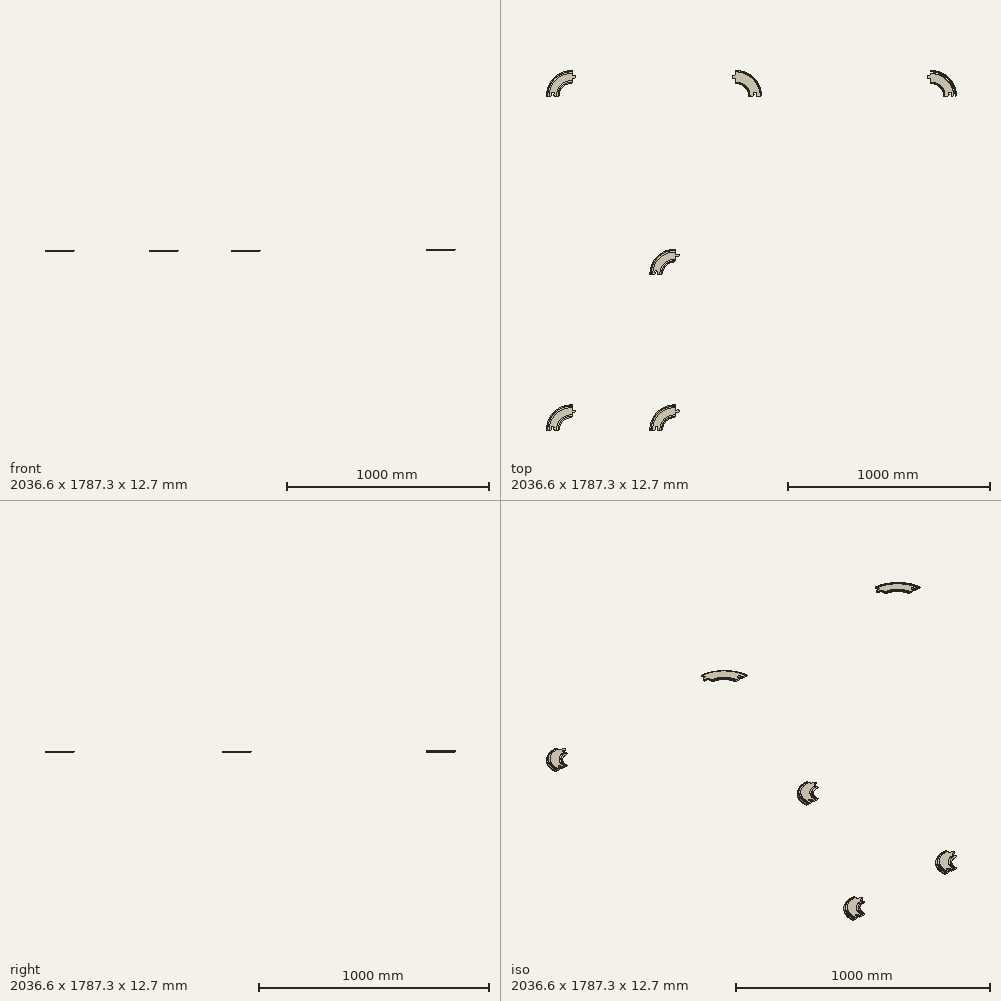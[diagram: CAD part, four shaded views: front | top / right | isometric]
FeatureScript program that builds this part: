
annotation { "Feature Type Name" : "Feature", "Feature Type Description" : "" }
export const myFeature = defineFeature(function(context is Context, id is Id, definition is map)
    precondition{}
    {
        {
            var Q0;
            Q0=qCreatedBy(makeId("Top.planeOp"),FACE);
            var sketch = newSketch(context, id + "F0", { "sketchPlane" : qUnion([Q0])});
            skArc(sketch, "E0", {"start": v(0, 127) * mm, "mid": v(-89.8, 89.8) * mm, "end": v(-127, 0) * mm});
            skArc(sketch, "E1.0", {"start": v(0, 63.5) * mm, "mid": v(-44.9, 44.9) * mm, "end": v(-63.5, 0) * mm});
            skLineSegment(sketch, "E2", {"start": v(-127, 0) * mm, "end": v(-101.6, 0) * mm});
            skLineSegment(sketch, "E3", {"start": v(0, 63.5) * mm, "end": v(0, 88.9) * mm});
            skArc(sketch, "E4", {"start": v(12.7, 88.9) * mm, "mid": v(19.05, 95.25) * mm, "end": v(12.7, 101.6) * mm});
            skPoint(sketch, "E5.start.orphan", {"position": v(12.7, 62.67) * mm});
            skArc(sketch, "E6", {"start": v(12.7, 88.9) * mm, "mid": v(6.35, 90.29) * mm, "end": v(0, 88.9) * mm});
            skArc(sketch, "E7.MirrorCS", {"start": v(12.7, 101.6) * mm, "mid": v(6.35, 100.21) * mm, "end": v(0, 101.6) * mm});
            skArc(sketch, "E8", {"start": v(-88.9, 12.7) * mm, "mid": v(-95.25, 19.05) * mm, "end": v(-101.6, 12.7) * mm});
            skLineSegment(sketch, "E9", {"start": v(-101.6, 12.7) * mm, "end": v(-102.39, 12.7) * mm});
            skPoint(sketch, "E10.startSnap0", {"position": v(-102.39, 12.7) * mm});
            skPoint(sketch, "E11.orphan", {"position": v(-71.93, 12.7) * mm});
            skLineSegment(sketch, "E12.trimOffspring", {"start": v(-126.36, 12.7) * mm, "end": v(-132.85, 12.7) * mm});
            skArc(sketch, "E13", {"start": v(-88.9, 12.7) * mm, "mid": v(-90.29, 6.35) * mm, "end": v(-88.9, 0) * mm});
            skArc(sketch, "E14.MirrorCS", {"start": v(-101.6, 12.7) * mm, "mid": v(-100.21, 6.35) * mm, "end": v(-101.6, 0) * mm});
            skPoint(sketch, "E10.end.orphan", {"position": v(-101.6, 0) * mm});
            skLineSegment(sketch, "E15.trimOffspring", {"start": v(0, 101.6) * mm, "end": v(0, 127) * mm});
            skLineSegment(sketch, "E16.trimOffspring", {"start": v(-88.9, 0) * mm, "end": v(-63.5, 0) * mm});
            skLineSegment(sketch, "E17", {"start": v(76.77, 161.45) * mm, "end": v(76.77, -32.66) * mm});
            skLineSegment(sketch, "E18", {"start": v(333.5, 184.4) * mm, "end": v(333.5, -54.92) * mm});
            skLineSegment(sketch, "E19.MirrorCS", {"start": v(411.86, 12.7) * mm, "end": v(411.07, 12.7) * mm});
            skArc(sketch, "E20.MirrorCS", {"start": v(526.16, 88.9) * mm, "mid": v(519.8, 90.29) * mm, "end": v(513.46, 88.9) * mm});
            skArc(sketch, "E21.MirrorCS", {"start": v(526.16, 101.6) * mm, "mid": v(519.8, 100.21) * mm, "end": v(513.46, 101.6) * mm});
            skArc(sketch, "E22.MirrorCS", {"start": v(411.86, 12.7) * mm, "mid": v(413.24, 6.35) * mm, "end": v(411.86, 0) * mm});
            skArc(sketch, "E23.MirrorCS", {"start": v(424.56, 12.7) * mm, "mid": v(418.2, 19.05) * mm, "end": v(411.86, 12.7) * mm});
            skArc(sketch, "E24.MirrorCS", {"start": v(526.16, 88.9) * mm, "mid": v(532.5, 95.25) * mm, "end": v(526.16, 101.6) * mm});
            skLineSegment(sketch, "E25.MirrorCS", {"start": v(513.46, 63.5) * mm, "end": v(513.46, 88.9) * mm});
            skArc(sketch, "E26.MirrorCS", {"start": v(424.56, 12.7) * mm, "mid": v(423.17, 6.35) * mm, "end": v(424.56, 0) * mm});
            skLineSegment(sketch, "E27.MirrorCS", {"start": v(513.46, 101.6) * mm, "end": v(513.46, 127) * mm});
            skLineSegment(sketch, "E28.MirrorCS", {"start": v(424.56, 0) * mm, "end": v(449.96, 0) * mm});
            skPoint(sketch, "E29.MirrorP", {"position": v(526.16, 62.67) * mm});
            skLineSegment(sketch, "E30.MirrorCS", {"start": v(387.1, 12.7) * mm, "end": v(380.6, 12.7) * mm});
            skLineSegment(sketch, "E31.MirrorCS", {"start": v(386.46, 0) * mm, "end": v(411.86, 0) * mm});
            skPoint(sketch, "E32.MirrorP", {"position": v(411.07, 12.7) * mm});
            skArc(sketch, "E33.MirrorCS", {"start": v(513.46, 127) * mm, "mid": v(423.65, 89.8) * mm, "end": v(386.46, 0) * mm});
            skPoint(sketch, "E34.MirrorP", {"position": v(411.86, 0) * mm});
            skArc(sketch, "E35.MirrorCS", {"start": v(513.46, 63.5) * mm, "mid": v(468.55, 44.9) * mm, "end": v(449.96, 0) * mm});
            skPoint(sketch, "E36.MirrorP", {"position": v(441.53, 12.7) * mm});
            skLineSegment(sketch, "E37.MirrorCS", {"start": v(-101.6, -874.4) * mm, "end": v(-102.39, -874.4) * mm});
            skLineSegment(sketch, "E38.MirrorCS", {"start": v(411.86, -874.4) * mm, "end": v(411.07, -874.4) * mm});
            skArc(sketch, "E39.MirrorCS", {"start": v(424.56, -874.4) * mm, "mid": v(423.17, -880.75) * mm, "end": v(424.56, -887.1) * mm});
            skArc(sketch, "E40.MirrorCS", {"start": v(526.16, -785.5) * mm, "mid": v(519.8, -786.88) * mm, "end": v(513.46, -785.5) * mm});
            skArc(sketch, "E41.MirrorCS", {"start": v(-101.6, -874.4) * mm, "mid": v(-100.21, -880.75) * mm, "end": v(-101.6, -887.1) * mm});
            skArc(sketch, "E42.MirrorCS", {"start": v(424.56, -874.4) * mm, "mid": v(418.2, -868.05) * mm, "end": v(411.86, -874.4) * mm});
            skArc(sketch, "E43.MirrorCS", {"start": v(526.16, -798.2) * mm, "mid": v(519.8, -796.81) * mm, "end": v(513.46, -798.2) * mm});
            skArc(sketch, "E44.MirrorCS", {"start": v(411.86, -874.4) * mm, "mid": v(413.24, -880.75) * mm, "end": v(411.86, -887.1) * mm});
            skArc(sketch, "E45.MirrorCS", {"start": v(-88.9, -874.4) * mm, "mid": v(-90.29, -880.75) * mm, "end": v(-88.9, -887.1) * mm});
            skArc(sketch, "E46.MirrorCS", {"start": v(-88.9, -874.4) * mm, "mid": v(-95.25, -868.05) * mm, "end": v(-101.6, -874.4) * mm});
            skLineSegment(sketch, "E47.MirrorCS", {"start": v(424.56, -887.1) * mm, "end": v(449.96, -887.1) * mm});
            skArc(sketch, "E48.MirrorCS", {"start": v(526.16, -798.2) * mm, "mid": v(532.5, -791.85) * mm, "end": v(526.16, -785.5) * mm});
            skArc(sketch, "E49.MirrorCS", {"start": v(12.7, -798.2) * mm, "mid": v(19.05, -791.85) * mm, "end": v(12.7, -785.5) * mm});
            skArc(sketch, "E50.MirrorCS", {"start": v(12.7, -785.5) * mm, "mid": v(6.35, -786.88) * mm, "end": v(0, -785.5) * mm});
            skArc(sketch, "E51.MirrorCS", {"start": v(12.7, -798.2) * mm, "mid": v(6.35, -796.81) * mm, "end": v(0, -798.2) * mm});
            skLineSegment(sketch, "E52.MirrorCS", {"start": v(-127, -887.1) * mm, "end": v(-101.6, -887.1) * mm});
            skLineSegment(sketch, "E53.MirrorCS", {"start": v(-88.9, -887.1) * mm, "end": v(-63.5, -887.1) * mm});
            skLineSegment(sketch, "E54.MirrorCS", {"start": v(-126.36, -874.4) * mm, "end": v(-132.85, -874.4) * mm});
            skLineSegment(sketch, "E55.MirrorCS", {"start": v(513.46, -823.6) * mm, "end": v(513.46, -798.2) * mm});
            skLineSegment(sketch, "E56.MirrorCS", {"start": v(387.1, -874.4) * mm, "end": v(380.6, -874.4) * mm});
            skLineSegment(sketch, "E57.MirrorCS", {"start": v(513.46, -785.5) * mm, "end": v(513.46, -760.1) * mm});
            skLineSegment(sketch, "E58.MirrorCS", {"start": v(0, -785.5) * mm, "end": v(0, -760.1) * mm});
            skLineSegment(sketch, "E59.MirrorCS", {"start": v(0, -823.6) * mm, "end": v(0, -798.2) * mm});
            skLineSegment(sketch, "E60.MirrorCS", {"start": v(386.46, -887.1) * mm, "end": v(411.86, -887.1) * mm});
            skPoint(sketch, "E61.MirrorP", {"position": v(526.16, -824.42) * mm});
            skPoint(sketch, "E62.MirrorP", {"position": v(-71.93, -874.4) * mm});
            skPoint(sketch, "E63.MirrorP", {"position": v(-101.6, -887.1) * mm});
            skArc(sketch, "E64.MirrorCS", {"start": v(0, -823.6) * mm, "mid": v(-44.9, -842.2) * mm, "end": v(-63.5, -887.1) * mm});
            skLineSegment(sketch, "E65.MirrorCS", {"start": v(333.5, -702.69) * mm, "end": v(333.5, -942.02) * mm});
            skArc(sketch, "E66.MirrorCS", {"start": v(513.46, -823.6) * mm, "mid": v(468.55, -842.2) * mm, "end": v(449.96, -887.1) * mm});
            skArc(sketch, "E67.MirrorCS", {"start": v(513.46, -760.1) * mm, "mid": v(423.65, -797.3) * mm, "end": v(386.46, -887.1) * mm});
            skPoint(sketch, "E68.MirrorP", {"position": v(411.86, -887.1) * mm});
            skPoint(sketch, "E69.MirrorP", {"position": v(441.53, -874.4) * mm});
            skArc(sketch, "E70.MirrorCS", {"start": v(0, -760.1) * mm, "mid": v(-89.8, -797.3) * mm, "end": v(-127, -887.1) * mm});
            skPoint(sketch, "E71.MirrorP", {"position": v(12.7, -824.42) * mm});
            skPoint(sketch, "E72.MirrorP", {"position": v(-102.39, -874.4) * mm});
            skLineSegment(sketch, "E73.MirrorCS", {"start": v(76.77, -725.65) * mm, "end": v(76.77, -919.76) * mm});
            skPoint(sketch, "E74.MirrorP", {"position": v(411.07, -874.4) * mm});
            skLineSegment(sketch, "E75.MirrorCS", {"start": v(411.86, -1647.6) * mm, "end": v(411.07, -1647.6) * mm});
            skArc(sketch, "E76.MirrorCS", {"start": v(424.56, -1647.6) * mm, "mid": v(418.2, -1641.26) * mm, "end": v(411.86, -1647.6) * mm});
            skArc(sketch, "E77.MirrorCS", {"start": v(424.56, -1647.6) * mm, "mid": v(423.17, -1653.96) * mm, "end": v(424.56, -1660.3) * mm});
            skArc(sketch, "E78.MirrorCS", {"start": v(411.86, -1647.6) * mm, "mid": v(413.24, -1653.96) * mm, "end": v(411.86, -1660.3) * mm});
            skLineSegment(sketch, "E79.MirrorCS", {"start": v(386.46, -1660.3) * mm, "end": v(411.86, -1660.3) * mm});
            skArc(sketch, "E80.MirrorCS", {"start": v(-88.9, -1647.6) * mm, "mid": v(-90.29, -1653.96) * mm, "end": v(-88.9, -1660.3) * mm});
            skLineSegment(sketch, "E81.MirrorCS", {"start": v(-127, -1660.3) * mm, "end": v(-101.6, -1660.3) * mm});
            skLineSegment(sketch, "E82.MirrorCS", {"start": v(-101.6, -1647.6) * mm, "end": v(-102.39, -1647.6) * mm});
            skArc(sketch, "E83.MirrorCS", {"start": v(-101.6, -1647.6) * mm, "mid": v(-100.21, -1653.96) * mm, "end": v(-101.6, -1660.3) * mm});
            skArc(sketch, "E84.MirrorCS", {"start": v(-88.9, -1647.6) * mm, "mid": v(-95.25, -1641.26) * mm, "end": v(-101.6, -1647.6) * mm});
            skArc(sketch, "E85.MirrorCS", {"start": v(526.16, -1571.4) * mm, "mid": v(519.8, -1570.02) * mm, "end": v(513.46, -1571.4) * mm});
            skArc(sketch, "E86.MirrorCS", {"start": v(526.16, -1558.7) * mm, "mid": v(519.8, -1560.1) * mm, "end": v(513.46, -1558.7) * mm});
            skLineSegment(sketch, "E87.MirrorCS", {"start": v(513.46, -1596.8) * mm, "end": v(513.46, -1571.4) * mm});
            skArc(sketch, "E88.MirrorCS", {"start": v(526.16, -1571.4) * mm, "mid": v(532.5, -1565.06) * mm, "end": v(526.16, -1558.7) * mm});
            skArc(sketch, "E89.MirrorCS", {"start": v(12.7, -1571.4) * mm, "mid": v(19.05, -1565.06) * mm, "end": v(12.7, -1558.7) * mm});
            skArc(sketch, "E90.MirrorCS", {"start": v(12.7, -1571.4) * mm, "mid": v(6.35, -1570.02) * mm, "end": v(0, -1571.4) * mm});
            skArc(sketch, "E91.MirrorCS", {"start": v(12.7, -1558.7) * mm, "mid": v(6.35, -1560.1) * mm, "end": v(0, -1558.7) * mm});
            skLineSegment(sketch, "E92.MirrorCS", {"start": v(-88.9, -1660.3) * mm, "end": v(-63.5, -1660.3) * mm});
            skLineSegment(sketch, "E93.MirrorCS", {"start": v(424.56, -1660.3) * mm, "end": v(449.96, -1660.3) * mm});
            skLineSegment(sketch, "E94.MirrorCS", {"start": v(513.46, -1558.7) * mm, "end": v(513.46, -1533.3) * mm});
            skLineSegment(sketch, "E95.MirrorCS", {"start": v(0, -1596.8) * mm, "end": v(0, -1571.4) * mm});
            skLineSegment(sketch, "E96.MirrorCS", {"start": v(-126.36, -1647.6) * mm, "end": v(-132.85, -1647.6) * mm});
            skLineSegment(sketch, "E97.MirrorCS", {"start": v(387.1, -1647.6) * mm, "end": v(380.6, -1647.6) * mm});
            skLineSegment(sketch, "E98.MirrorCS", {"start": v(0, -1558.7) * mm, "end": v(0, -1533.3) * mm});
            skPoint(sketch, "E99.MirrorP", {"position": v(526.16, -1597.64) * mm});
            skArc(sketch, "E100.MirrorCS", {"start": v(0, -1533.3) * mm, "mid": v(-89.8, -1570.5) * mm, "end": v(-127, -1660.3) * mm});
            skPoint(sketch, "E101.MirrorP", {"position": v(441.53, -1647.6) * mm});
            skArc(sketch, "E102.MirrorCS", {"start": v(513.46, -1596.8) * mm, "mid": v(468.55, -1615.4) * mm, "end": v(449.96, -1660.3) * mm});
            skPoint(sketch, "E103.MirrorP", {"position": v(411.07, -1647.6) * mm});
            skPoint(sketch, "E104.MirrorP", {"position": v(411.86, -1660.3) * mm});
            skPoint(sketch, "E105.MirrorP", {"position": v(-71.93, -1647.6) * mm});
            skPoint(sketch, "E106.MirrorP", {"position": v(-102.39, -1647.6) * mm});
            skLineSegment(sketch, "E107.MirrorCS", {"start": v(333.5, -1475.9) * mm, "end": v(333.5, -1715.23) * mm});
            skPoint(sketch, "E108.MirrorP", {"position": v(-101.6, -1660.3) * mm});
            skArc(sketch, "E109.MirrorCS", {"start": v(513.46, -1533.3) * mm, "mid": v(423.65, -1570.5) * mm, "end": v(386.46, -1660.3) * mm});
            skLineSegment(sketch, "E110.MirrorCS", {"start": v(76.77, -1498.86) * mm, "end": v(76.77, -1692.97) * mm});
            skPoint(sketch, "E111.MirrorP", {"position": v(12.7, -1597.64) * mm});
            skArc(sketch, "E112.MirrorCS", {"start": v(0, -1596.8) * mm, "mid": v(-44.9, -1615.4) * mm, "end": v(-63.5, -1660.3) * mm});
            skLineSegment(sketch, "E113", {"start": v(663.76, 185.94) * mm, "end": v(663.76, -109.84) * mm});
            skLineSegment(sketch, "E114", {"start": v(308.83, -128.2) * mm, "end": v(873.87, -128.2) * mm});
            skArc(sketch, "E115.MirrorCS", {"start": v(915.67, 12.7) * mm, "mid": v(914.28, 6.35) * mm, "end": v(915.67, 0) * mm});
            skArc(sketch, "E116.MirrorCS", {"start": v(902.97, 12.7) * mm, "mid": v(909.32, 19.05) * mm, "end": v(915.67, 12.7) * mm});
            skArc(sketch, "E117.MirrorCS", {"start": v(902.97, 12.7) * mm, "mid": v(904.35, 6.35) * mm, "end": v(902.97, 0) * mm});
            skLineSegment(sketch, "E118.MirrorCS", {"start": v(915.67, 12.7) * mm, "end": v(916.46, 12.7) * mm});
            skArc(sketch, "E119.MirrorCS", {"start": v(801.37, 88.9) * mm, "mid": v(807.72, 90.29) * mm, "end": v(814.07, 88.9) * mm});
            skArc(sketch, "E120.MirrorCS", {"start": v(801.37, 101.6) * mm, "mid": v(807.72, 100.21) * mm, "end": v(814.07, 101.6) * mm});
            skLineSegment(sketch, "E121.MirrorCS", {"start": v(814.07, 63.5) * mm, "end": v(814.07, 88.9) * mm});
            skArc(sketch, "E122.MirrorCS", {"start": v(801.37, 88.9) * mm, "mid": v(795.02, 95.25) * mm, "end": v(801.37, 101.6) * mm});
            skLineSegment(sketch, "E123.MirrorCS", {"start": v(814.07, 101.6) * mm, "end": v(814.07, 127) * mm});
            skLineSegment(sketch, "E124.MirrorCS", {"start": v(941.07, 0) * mm, "end": v(915.67, 0) * mm});
            skLineSegment(sketch, "E125.MirrorCS", {"start": v(902.97, 0) * mm, "end": v(877.57, 0) * mm});
            skLineSegment(sketch, "E126.MirrorCS", {"start": v(940.43, 12.7) * mm, "end": v(946.92, 12.7) * mm});
            skPoint(sketch, "E127.MirrorP", {"position": v(801.37, 62.67) * mm});
            skPoint(sketch, "E128.MirrorP", {"position": v(916.46, 12.7) * mm});
            skArc(sketch, "E129.MirrorCS", {"start": v(814.07, 63.5) * mm, "mid": v(858.97, 44.9) * mm, "end": v(877.57, 0) * mm});
            skArc(sketch, "E130.MirrorCS", {"start": v(814.07, 127) * mm, "mid": v(903.87, 89.8) * mm, "end": v(941.07, 0) * mm});
            skPoint(sketch, "E131.MirrorP", {"position": v(915.67, 0) * mm});
            skPoint(sketch, "E132.MirrorP", {"position": v(886, 12.7) * mm});
            skArc(sketch, "E133.MirrorCS", {"start": v(424.56, -269.1) * mm, "mid": v(423.17, -262.75) * mm, "end": v(424.56, -256.4) * mm});
            skArc(sketch, "E134.MirrorCS", {"start": v(526.16, -345.3) * mm, "mid": v(519.8, -346.68) * mm, "end": v(513.46, -345.3) * mm});
            skArc(sketch, "E135.MirrorCS", {"start": v(411.86, -269.1) * mm, "mid": v(413.24, -262.75) * mm, "end": v(411.86, -256.4) * mm});
            skLineSegment(sketch, "E136.MirrorCS", {"start": v(411.86, -269.1) * mm, "end": v(411.07, -269.1) * mm});
            skArc(sketch, "E137.MirrorCS", {"start": v(526.16, -358) * mm, "mid": v(519.8, -356.61) * mm, "end": v(513.46, -358) * mm});
            skArc(sketch, "E138.MirrorCS", {"start": v(424.56, -269.1) * mm, "mid": v(418.2, -275.45) * mm, "end": v(411.86, -269.1) * mm});
            skArc(sketch, "E139.MirrorCS", {"start": v(526.16, -345.3) * mm, "mid": v(532.5, -351.65) * mm, "end": v(526.16, -358) * mm});
            skLineSegment(sketch, "E140.MirrorCS", {"start": v(424.56, -256.4) * mm, "end": v(449.96, -256.4) * mm});
            skLineSegment(sketch, "E141.MirrorCS", {"start": v(513.46, -319.9) * mm, "end": v(513.46, -345.3) * mm});
            skLineSegment(sketch, "E142.MirrorCS", {"start": v(387.1, -269.1) * mm, "end": v(380.6, -269.1) * mm});
            skLineSegment(sketch, "E143.MirrorCS", {"start": v(386.46, -256.4) * mm, "end": v(411.86, -256.4) * mm});
            skLineSegment(sketch, "E144.MirrorCS", {"start": v(513.46, -358) * mm, "end": v(513.46, -383.4) * mm});
            skPoint(sketch, "E145.MirrorP", {"position": v(526.16, -319.07) * mm});
            skArc(sketch, "E146.MirrorCS", {"start": v(513.46, -383.4) * mm, "mid": v(423.65, -346.2) * mm, "end": v(386.46, -256.4) * mm});
            skArc(sketch, "E147.MirrorCS", {"start": v(513.46, -319.9) * mm, "mid": v(468.55, -301.3) * mm, "end": v(449.96, -256.4) * mm});
            skPoint(sketch, "E148.MirrorP", {"position": v(411.86, -256.4) * mm});
            skPoint(sketch, "E149.MirrorP", {"position": v(441.53, -269.1) * mm});
            skPoint(sketch, "E150.MirrorP", {"position": v(411.07, -269.1) * mm});
            skSolve(sketch);
        }
        {
            var Q0;
            Q0=makeQuery(id+"F0.imprint","IMPRINT",FACE,{"disambiguationData":[TD([[makeQuery(id+"F0.imprint","IMPRINT",EDGE,{"derivedFrom":sQuery(id+"F0.wireOp",EDGE,"E1.0")}),-1.0]])]});
            var Q1;
            Q1=makeQuery(id+"F0.imprint","IMPRINT",FACE,{"disambiguationData":[TD([[makeQuery(id+"F0.imprint","IMPRINT",EDGE,{"derivedFrom":sQuery(id+"F0.wireOp",EDGE,"E22.MirrorCS")}),-1.0]])]});
            var Q2;
            Q2=makeQuery(id+"F0.imprint","IMPRINT",FACE,{"disambiguationData":[TD([[makeQuery(id+"F0.imprint","IMPRINT",EDGE,{"derivedFrom":sQuery(id+"F0.wireOp",EDGE,"E39.MirrorCS")}),1.0]])]});
            var Q3;
            Q3=makeQuery(id+"F0.imprint","IMPRINT",FACE,{"disambiguationData":[TD([[makeQuery(id+"F0.imprint","IMPRINT",EDGE,{"derivedFrom":sQuery(id+"F0.wireOp",EDGE,"E41.MirrorCS")}),-1.0]])]});
            var Q4;
            Q4=makeQuery(id+"F0.imprint","IMPRINT",FACE,{"disambiguationData":[TD([[makeQuery(id+"F0.imprint","IMPRINT",EDGE,{"derivedFrom":sQuery(id+"F0.wireOp",EDGE,"E80.MirrorCS")}),1.0]])]});
            var Q5;
            Q5=makeQuery(id+"F0.imprint","IMPRINT",FACE,{"disambiguationData":[TD([[makeQuery(id+"F0.imprint","IMPRINT",EDGE,{"derivedFrom":sQuery(id+"F0.wireOp",EDGE,"E115.MirrorCS")}),1.0]])]});
            var Q6;
            Q6=makeQuery(id+"F0.imprint","IMPRINT",FACE,{"disambiguationData":[TD([[makeQuery(id+"F0.imprint","IMPRINT",EDGE,{"derivedFrom":sQuery(id+"F0.wireOp",EDGE,"E133.MirrorCS")}),-1.0]])]});
            var Q7;
            Q7=makeQuery(id+"F0.imprint","IMPRINT",FACE,{"disambiguationData":[TD([[makeQuery(id+"F0.imprint","IMPRINT",EDGE,{"derivedFrom":sQuery(id+"F0.wireOp",EDGE,"E76.MirrorCS")}),-1.0]])]});
            extrude(context, id + "F1", {"entities" : qUnion([Q0, Q1, Q2, Q3, Q4, Q5, Q6, Q7]), "depth" : 6.35 * mm});
        }
        {
            var Q0;
            Q0=makeQuery(id+"F1.opExtrude","CAP_FACE",FACE,{"disambiguationData":[OSD([sQuery(id+"F0.wireOp",EDGE,"E0"),sQuery(id+"F0.wireOp",EDGE,"E1.0"),sQuery(id+"F0.wireOp",EDGE,"E2"),sQuery(id+"F0.wireOp",EDGE,"E3"),sQuery(id+"F0.wireOp",EDGE,"E4"),sQuery(id+"F0.wireOp",EDGE,"E6"),sQuery(id+"F0.wireOp",EDGE,"E7.MirrorCS"),sQuery(id+"F0.wireOp",EDGE,"E8"),sQuery(id+"F0.wireOp",EDGE,"E13"),sQuery(id+"F0.wireOp",EDGE,"E14.MirrorCS"),sQuery(id+"F0.wireOp",EDGE,"E15.trimOffspring"),sQuery(id+"F0.wireOp",EDGE,"E16.trimOffspring")])],"isStart":false});
            var sketch = newSketch(context, id + "F2", { "sketchPlane" : qUnion([Q0])});
            skArc(sketch, "E151.0", {"start": v(0, 63.5) * mm, "mid": v(-44.9, 44.9) * mm, "end": v(-63.5, 0) * mm});
            skArc(sketch, "E151.1", {"start": v(0, 127) * mm, "mid": v(-89.8, 89.8) * mm, "end": v(-127, 0) * mm});
            skLineSegment(sketch, "E152.0", {"start": v(76.77, 161.45) * mm, "end": v(76.77, -32.66) * mm});
            skLineSegment(sketch, "E152.1", {"start": v(333.5, 184.4) * mm, "end": v(333.5, -54.92) * mm});
            skArc(sketch, "E153.0", {"start": v(0, 69.85) * mm, "mid": v(-49.4, 49.4) * mm, "end": v(-69.85, 0) * mm});
            skArc(sketch, "E154.0", {"start": v(0, 77.47) * mm, "mid": v(-54.78, 54.78) * mm, "end": v(-77.47, 0) * mm});
            skArc(sketch, "E155.0", {"start": v(0, 120.65) * mm, "mid": v(-85.31, 85.31) * mm, "end": v(-120.65, 0) * mm});
            skArc(sketch, "E156.0", {"start": v(0, 113.03) * mm, "mid": v(-79.92, 79.92) * mm, "end": v(-113.03, 0) * mm});
            skArc(sketch, "E157.MirrorCS", {"start": v(153.53, 113.03) * mm, "mid": v(233.46, 79.92) * mm, "end": v(266.56, 0) * mm});
            skArc(sketch, "E158.MirrorCS", {"start": v(153.53, 120.65) * mm, "mid": v(238.85, 85.31) * mm, "end": v(274.18, 0) * mm});
            skArc(sketch, "E159.MirrorCS", {"start": v(153.53, 69.85) * mm, "mid": v(202.93, 49.4) * mm, "end": v(223.38, 0) * mm});
            skArc(sketch, "E160.MirrorCS", {"start": v(153.53, 77.47) * mm, "mid": v(208.31, 54.78) * mm, "end": v(231, 0) * mm});
            skArc(sketch, "E161.MirrorCS", {"start": v(513.46, 120.65) * mm, "mid": v(428.14, 85.31) * mm, "end": v(392.8, 0) * mm});
            skArc(sketch, "E162.MirrorCS", {"start": v(513.46, 113.03) * mm, "mid": v(433.53, 79.92) * mm, "end": v(400.43, 0) * mm});
            skArc(sketch, "E163.MirrorCS", {"start": v(513.46, 69.85) * mm, "mid": v(464.06, 49.4) * mm, "end": v(443.6, 0) * mm});
            skArc(sketch, "E164.MirrorCS", {"start": v(513.46, 77.47) * mm, "mid": v(458.68, 54.78) * mm, "end": v(435.99, 0) * mm});
            skArc(sketch, "E165.MirrorCS", {"start": v(0, -403.9) * mm, "mid": v(-54.78, -381.21) * mm, "end": v(-77.47, -326.43) * mm});
            skArc(sketch, "E166.MirrorCS", {"start": v(0, -396.28) * mm, "mid": v(-49.4, -375.82) * mm, "end": v(-69.85, -326.43) * mm});
            skArc(sketch, "E167.MirrorCS", {"start": v(0, -447.08) * mm, "mid": v(-85.31, -411.74) * mm, "end": v(-120.65, -326.43) * mm});
            skLineSegment(sketch, "E168.MirrorCS", {"start": v(333.5, -510.84) * mm, "end": v(333.5, -271.5) * mm});
            skArc(sketch, "E169.MirrorCS", {"start": v(0, -439.46) * mm, "mid": v(-79.92, -406.36) * mm, "end": v(-113.03, -326.43) * mm});
            skArc(sketch, "E170.MirrorCS", {"start": v(153.53, -439.46) * mm, "mid": v(233.46, -406.36) * mm, "end": v(266.56, -326.43) * mm});
            skLineSegment(sketch, "E171.MirrorCS", {"start": v(76.77, -487.88) * mm, "end": v(76.77, -293.77) * mm});
            skArc(sketch, "E172.MirrorCS", {"start": v(0, -453.43) * mm, "mid": v(-89.8, -416.23) * mm, "end": v(-127, -326.43) * mm});
            skArc(sketch, "E173.MirrorCS", {"start": v(153.53, -447.08) * mm, "mid": v(238.85, -411.74) * mm, "end": v(274.18, -326.43) * mm});
            skArc(sketch, "E174.MirrorCS", {"start": v(0, -389.93) * mm, "mid": v(-44.9, -371.33) * mm, "end": v(-63.5, -326.43) * mm});
            skArc(sketch, "E175.MirrorCS", {"start": v(513.46, -396.28) * mm, "mid": v(464.06, -375.82) * mm, "end": v(443.6, -326.43) * mm});
            skArc(sketch, "E176.MirrorCS", {"start": v(153.53, -396.28) * mm, "mid": v(202.93, -375.82) * mm, "end": v(223.38, -326.43) * mm});
            skArc(sketch, "E177.MirrorCS", {"start": v(153.53, -403.9) * mm, "mid": v(208.31, -381.21) * mm, "end": v(231, -326.43) * mm});
            skArc(sketch, "E178.MirrorCS", {"start": v(513.46, -439.46) * mm, "mid": v(433.53, -406.36) * mm, "end": v(400.43, -326.43) * mm});
            skArc(sketch, "E179.MirrorCS", {"start": v(513.46, -447.08) * mm, "mid": v(428.14, -411.74) * mm, "end": v(392.8, -326.43) * mm});
            skArc(sketch, "E180.MirrorCS", {"start": v(513.46, -403.9) * mm, "mid": v(458.68, -381.21) * mm, "end": v(435.99, -326.43) * mm});
            skLineSegment(sketch, "E181", {"start": v(-77.47, 0) * mm, "end": v(-69.85, 0) * mm});
            skLineSegment(sketch, "E182", {"start": v(-113.03, 0) * mm, "end": v(-120.65, 0) * mm});
            skLineSegment(sketch, "E183", {"start": v(0, 69.85) * mm, "end": v(0, 77.47) * mm});
            skLineSegment(sketch, "E184", {"start": v(0, 113.03) * mm, "end": v(0, 120.65) * mm});
            skLineSegment(sketch, "E185", {"start": v(153.53, 77.47) * mm, "end": v(153.53, 69.85) * mm});
            skLineSegment(sketch, "E186", {"start": v(153.53, 113.03) * mm, "end": v(153.53, 120.65) * mm});
            skLineSegment(sketch, "E187", {"start": v(223.38, 0) * mm, "end": v(231, 0) * mm});
            skLineSegment(sketch, "E188", {"start": v(266.56, 0) * mm, "end": v(274.18, 0) * mm});
            skLineSegment(sketch, "E189", {"start": v(392.8, 0) * mm, "end": v(400.43, 0) * mm});
            skLineSegment(sketch, "E190", {"start": v(435.99, 0) * mm, "end": v(443.6, 0) * mm});
            skLineSegment(sketch, "E191", {"start": v(513.46, 69.85) * mm, "end": v(513.46, 77.47) * mm});
            skLineSegment(sketch, "E192", {"start": v(513.46, 120.65) * mm, "end": v(513.46, 113.03) * mm});
            skLineSegment(sketch, "E193", {"start": v(392.8, -326.43) * mm, "end": v(400.43, -326.43) * mm});
            skLineSegment(sketch, "E194", {"start": v(435.99, -326.43) * mm, "end": v(443.6, -326.43) * mm});
            skLineSegment(sketch, "E195", {"start": v(513.46, -396.28) * mm, "end": v(513.46, -403.9) * mm});
            skLineSegment(sketch, "E196", {"start": v(513.46, -447.08) * mm, "end": v(513.46, -439.46) * mm});
            skLineSegment(sketch, "E197", {"start": v(266.56, -326.43) * mm, "end": v(274.18, -326.43) * mm});
            skLineSegment(sketch, "E198", {"start": v(231, -326.43) * mm, "end": v(223.38, -326.43) * mm});
            skLineSegment(sketch, "E199", {"start": v(153.53, -396.28) * mm, "end": v(153.53, -403.9) * mm});
            skLineSegment(sketch, "E200", {"start": v(153.53, -439.46) * mm, "end": v(153.53, -447.08) * mm});
            skLineSegment(sketch, "E201", {"start": v(0, -403.9) * mm, "end": v(0, -396.28) * mm});
            skLineSegment(sketch, "E202", {"start": v(0, -447.08) * mm, "end": v(0, -439.46) * mm});
            skLineSegment(sketch, "E203", {"start": v(-69.85, -326.43) * mm, "end": v(-77.47, -326.43) * mm});
            skLineSegment(sketch, "E204", {"start": v(-113.03, -326.43) * mm, "end": v(-120.65, -326.43) * mm});
            skArc(sketch, "E205.0", {"start": v(0, -760.1) * mm, "mid": v(-89.8, -797.3) * mm, "end": v(-127, -887.1) * mm});
            skArc(sketch, "E205.1", {"start": v(0, -823.6) * mm, "mid": v(-44.9, -842.2) * mm, "end": v(-63.5, -887.1) * mm});
            skArc(sketch, "E205.2", {"start": v(513.46, -760.1) * mm, "mid": v(423.65, -797.3) * mm, "end": v(386.46, -887.1) * mm});
            skArc(sketch, "E205.3", {"start": v(513.46, -823.6) * mm, "mid": v(468.55, -842.2) * mm, "end": v(449.96, -887.1) * mm});
            skPoint(sketch, "E206.endSnap0", {"position": v(0, -606.77) * mm});
            skLineSegment(sketch, "E207.MirrorCS", {"start": v(0, -766.45) * mm, "end": v(0, -774.07) * mm});
            skLineSegment(sketch, "E208.MirrorCS", {"start": v(392.8, -887.1) * mm, "end": v(400.43, -887.1) * mm});
            skLineSegment(sketch, "E209.MirrorCS", {"start": v(0, -809.63) * mm, "end": v(0, -817.25) * mm});
            skLineSegment(sketch, "E210.MirrorCS", {"start": v(435.99, -887.1) * mm, "end": v(443.6, -887.1) * mm});
            skLineSegment(sketch, "E211.MirrorCS", {"start": v(513.46, -817.25) * mm, "end": v(513.46, -809.63) * mm});
            skLineSegment(sketch, "E212.MirrorCS", {"start": v(513.46, -766.45) * mm, "end": v(513.46, -774.07) * mm});
            skLineSegment(sketch, "E213.MirrorCS", {"start": v(-69.85, -887.1) * mm, "end": v(-77.47, -887.1) * mm});
            skLineSegment(sketch, "E214.MirrorCS", {"start": v(231, -887.1) * mm, "end": v(223.38, -887.1) * mm});
            skLineSegment(sketch, "E215.MirrorCS", {"start": v(153.53, -774.07) * mm, "end": v(153.53, -766.45) * mm});
            skLineSegment(sketch, "E216.MirrorCS", {"start": v(153.53, -817.25) * mm, "end": v(153.53, -809.63) * mm});
            skLineSegment(sketch, "E217.MirrorCS", {"start": v(266.56, -887.1) * mm, "end": v(274.18, -887.1) * mm});
            skLineSegment(sketch, "E218.MirrorCS", {"start": v(-113.03, -887.1) * mm, "end": v(-120.65, -887.1) * mm});
            skLineSegment(sketch, "E219.MirrorCS", {"start": v(333.5, -702.69) * mm, "end": v(333.5, -942.02) * mm});
            skLineSegment(sketch, "E220.MirrorCS", {"start": v(0, -760.1) * mm, "end": v(0, -453.43) * mm});
            skArc(sketch, "E221.MirrorCS", {"start": v(0, -774.07) * mm, "mid": v(-79.92, -807.17) * mm, "end": v(-113.03, -887.1) * mm});
            skArc(sketch, "E222.MirrorCS", {"start": v(513.46, -766.45) * mm, "mid": v(428.14, -801.79) * mm, "end": v(392.8, -887.1) * mm});
            skArc(sketch, "E223.MirrorCS", {"start": v(153.53, -774.07) * mm, "mid": v(233.46, -807.17) * mm, "end": v(266.56, -887.1) * mm});
            skLineSegment(sketch, "E224.MirrorCS", {"start": v(76.77, -725.65) * mm, "end": v(76.77, -919.76) * mm});
            skArc(sketch, "E225.MirrorCS", {"start": v(153.53, -766.45) * mm, "mid": v(238.85, -801.79) * mm, "end": v(274.18, -887.1) * mm});
            skArc(sketch, "E226.MirrorCS", {"start": v(153.53, -809.63) * mm, "mid": v(208.31, -832.32) * mm, "end": v(231, -887.1) * mm});
            skArc(sketch, "E227.MirrorCS", {"start": v(513.46, -817.25) * mm, "mid": v(464.06, -837.7) * mm, "end": v(443.6, -887.1) * mm});
            skArc(sketch, "E228.MirrorCS", {"start": v(0, -766.45) * mm, "mid": v(-85.31, -801.79) * mm, "end": v(-120.65, -887.1) * mm});
            skArc(sketch, "E229.MirrorCS", {"start": v(0, -817.25) * mm, "mid": v(-49.4, -837.7) * mm, "end": v(-69.85, -887.1) * mm});
            skArc(sketch, "E230.MirrorCS", {"start": v(0, -809.63) * mm, "mid": v(-54.78, -832.32) * mm, "end": v(-77.47, -887.1) * mm});
            skArc(sketch, "E231.MirrorCS", {"start": v(513.46, -809.63) * mm, "mid": v(458.68, -832.32) * mm, "end": v(435.99, -887.1) * mm});
            skArc(sketch, "E232.MirrorCS", {"start": v(513.46, -774.07) * mm, "mid": v(433.53, -807.17) * mm, "end": v(400.43, -887.1) * mm});
            skArc(sketch, "E233.MirrorCS", {"start": v(153.53, -817.25) * mm, "mid": v(202.93, -837.7) * mm, "end": v(223.38, -887.1) * mm});
            skArc(sketch, "E234.0", {"start": v(0, -1533.3) * mm, "mid": v(-89.8, -1570.5) * mm, "end": v(-127, -1660.3) * mm});
            skArc(sketch, "E235.0", {"start": v(0, -1590.46) * mm, "mid": v(-49.4, -1610.92) * mm, "end": v(-69.85, -1660.3) * mm});
            skArc(sketch, "E236.0", {"start": v(0, -1582.84) * mm, "mid": v(-54.78, -1605.53) * mm, "end": v(-77.47, -1660.3) * mm});
            skArc(sketch, "E237.0", {"start": v(513.46, -1533.3) * mm, "mid": v(423.65, -1570.5) * mm, "end": v(386.46, -1660.3) * mm});
            skArc(sketch, "E238.0", {"start": v(513.46, -1590.46) * mm, "mid": v(464.06, -1610.92) * mm, "end": v(443.6, -1660.3) * mm});
            skArc(sketch, "E239.0", {"start": v(513.46, -1582.84) * mm, "mid": v(458.68, -1605.53) * mm, "end": v(435.99, -1660.3) * mm});
            skArc(sketch, "E240.0", {"start": v(513.46, -1539.66) * mm, "mid": v(428.14, -1575) * mm, "end": v(392.8, -1660.3) * mm});
            skArc(sketch, "E241.0", {"start": v(513.46, -1547.28) * mm, "mid": v(433.53, -1580.39) * mm, "end": v(400.43, -1660.3) * mm});
            skLineSegment(sketch, "E242.0", {"start": v(0, -1660.3) * mm, "end": v(0, -1660.3) * mm});
            skArc(sketch, "E243.0", {"start": v(0, -1539.66) * mm, "mid": v(-85.31, -1575) * mm, "end": v(-120.65, -1660.3) * mm});
            skArc(sketch, "E244.0", {"start": v(0, -1547.28) * mm, "mid": v(-79.92, -1580.39) * mm, "end": v(-113.03, -1660.3) * mm});
            skLineSegment(sketch, "E245", {"start": v(0, -1547.28) * mm, "end": v(0, -1539.66) * mm});
            skLineSegment(sketch, "E246", {"start": v(-77.47, -1660.3) * mm, "end": v(-69.85, -1660.3) * mm});
            skLineSegment(sketch, "E247", {"start": v(-113.03, -1660.3) * mm, "end": v(-120.65, -1660.3) * mm});
            skLineSegment(sketch, "E248", {"start": v(0, -1590.46) * mm, "end": v(0, -1582.84) * mm});
            skLineSegment(sketch, "E249", {"start": v(400.43, -1660.3) * mm, "end": v(392.8, -1660.3) * mm});
            skLineSegment(sketch, "E250", {"start": v(435.99, -1660.3) * mm, "end": v(443.6, -1660.3) * mm});
            skLineSegment(sketch, "E251", {"start": v(513.46, -1590.46) * mm, "end": v(513.46, -1582.84) * mm});
            skLineSegment(sketch, "E252", {"start": v(513.46, -1547.28) * mm, "end": v(513.46, -1539.66) * mm});
            skSolve(sketch);
        }
        {
            var Q0;
            Q0=qSketchRegion(id+"F2",true);
            extrude(context, id + "F3", {"entities" : qUnion([Q0]), "operationType" : NewBodyOperationType.REMOVE, "oppositeDirection" : true, "depth" : 1.9 * mm});
        }
        {
            var Q0;
            Q0=makeQuery(id+"F1.opExtrude","CAP_FACE",FACE,{"disambiguationData":[OSD([sQuery(id+"F0.wireOp",EDGE,"E115.MirrorCS"),sQuery(id+"F0.wireOp",EDGE,"E116.MirrorCS"),sQuery(id+"F0.wireOp",EDGE,"E117.MirrorCS"),sQuery(id+"F0.wireOp",EDGE,"E121.MirrorCS"),sQuery(id+"F0.wireOp",EDGE,"E120.MirrorCS"),sQuery(id+"F0.wireOp",EDGE,"E122.MirrorCS"),sQuery(id+"F0.wireOp",EDGE,"E119.MirrorCS"),sQuery(id+"F0.wireOp",EDGE,"E123.MirrorCS"),sQuery(id+"F0.wireOp",EDGE,"E124.MirrorCS"),sQuery(id+"F0.wireOp",EDGE,"E125.MirrorCS"),sQuery(id+"F0.wireOp",EDGE,"E129.MirrorCS"),sQuery(id+"F0.wireOp",EDGE,"E130.MirrorCS")])],"isStart":false});
            var sketch = newSketch(context, id + "F4", { "sketchPlane" : qUnion([Q0])});
            skArc(sketch, "E253.0", {"start": v(814.07, 69.85) * mm, "mid": v(863.46, 49.4) * mm, "end": v(883.92, 0) * mm});
            skArc(sketch, "E254.0", {"start": v(814.07, 77.47) * mm, "mid": v(868.85, 54.78) * mm, "end": v(891.54, 0) * mm});
            skArc(sketch, "E255.0", {"start": v(814.07, 120.65) * mm, "mid": v(899.38, 85.31) * mm, "end": v(934.72, 0) * mm});
            skArc(sketch, "E256.0", {"start": v(814.07, 113.03) * mm, "mid": v(894, 79.92) * mm, "end": v(927.1, 0) * mm});
            skLineSegment(sketch, "E257", {"start": v(814.07, 120.65) * mm, "end": v(814.07, 113.03) * mm});
            skLineSegment(sketch, "E258", {"start": v(814.07, 77.47) * mm, "end": v(814.07, 69.85) * mm});
            skLineSegment(sketch, "E259", {"start": v(891.54, 0) * mm, "end": v(883.92, 0) * mm});
            skLineSegment(sketch, "E260", {"start": v(927.1, 0) * mm, "end": v(934.72, 0) * mm});
            skSolve(sketch);
        }
        {
            var Q0;
            Q0=makeQuery(id+"F4.imprint","IMPRINT",FACE,{"disambiguationData":[TD([[makeQuery(id+"F4.imprint","IMPRINT",EDGE,{"derivedFrom":sQuery(id+"F4.wireOp",EDGE,"E255.0")}),-1.0]])]});
            var Q1;
            Q1=makeQuery(id+"F4.imprint","IMPRINT",FACE,{"disambiguationData":[TD([[makeQuery(id+"F4.imprint","IMPRINT",EDGE,{"derivedFrom":sQuery(id+"F4.wireOp",EDGE,"E253.0")}),1.0]])]});
            extrude(context, id + "F5", {"entities" : qUnion([Q0, Q1]), "operationType" : NewBodyOperationType.REMOVE, "oppositeDirection" : true, "depth" : 1.9 * mm});
        }
        {
            var Q0;
            {var subQ0=sQuery(id+"F0.wireOp",EDGE,"E125.MirrorCS");var subQ1=sQuery(id+"F0.wireOp",EDGE,"E123.MirrorCS");var subQ2=sQuery(id+"F0.wireOp",EDGE,"E119.MirrorCS");var subQ3=sQuery(id+"F0.wireOp",EDGE,"E122.MirrorCS");var subQ4=sQuery(id+"F0.wireOp",EDGE,"E115.MirrorCS");var subQ5=sQuery(id+"F0.wireOp",EDGE,"E120.MirrorCS");var subQ6=sQuery(id+"F0.wireOp",EDGE,"E116.MirrorCS");var subQ7=sQuery(id+"F0.wireOp",EDGE,"E117.MirrorCS");var subQ8=sQuery(id+"F0.wireOp",EDGE,"E124.MirrorCS");var subQ9=sQuery(id+"F0.wireOp",EDGE,"E121.MirrorCS");Q0=makeQuery(id+"F5.boolean.opBoolean","SPLIT",FACE,{"disambiguationData":[TD([makeQuery(id+"F1.opExtrude","SWEPT_FACE",FACE,{"disambiguationData":[OSD([subQ4])]})])],"derivedFrom":makeQuery(id+"F1.opExtrude","CAP_FACE",FACE,{"disambiguationData":[OSD([subQ4,subQ6,subQ7,subQ9,subQ5,subQ3,subQ2,subQ1,subQ8,subQ0,sQuery(id+"F0.wireOp",EDGE,"E129.MirrorCS"),sQuery(id+"F0.wireOp",EDGE,"E130.MirrorCS")])],"isStart":false})});}
            var sketch = newSketch(context, id + "F6", { "sketchPlane" : qUnion([Q0])});
            skLineSegment(sketch, "E261", {"start": v(1034.93, 198.47) * mm, "end": v(1034.93, -110.58) * mm});
            skPoint(sketch, "E262.0", {"position": v(916.46, 12.7) * mm});
            skArc(sketch, "E262.1", {"start": v(814.07, 120.65) * mm, "mid": v(899.38, 85.31) * mm, "end": v(934.72, 0) * mm});
            skArc(sketch, "E262.2", {"start": v(814.07, 113.03) * mm, "mid": v(894, 79.92) * mm, "end": v(927.1, 0) * mm});
            skArc(sketch, "E262.3", {"start": v(814.07, 127) * mm, "mid": v(903.87, 89.8) * mm, "end": v(941.07, 0) * mm});
            skLineSegment(sketch, "E262.4", {"start": v(941.07, 0) * mm, "end": v(915.67, 0) * mm});
            skLineSegment(sketch, "E262.5", {"start": v(902.97, 0) * mm, "end": v(877.57, 0) * mm});
            skArc(sketch, "E262.6", {"start": v(902.97, 12.7) * mm, "mid": v(904.35, 6.35) * mm, "end": v(902.97, 0) * mm});
            skArc(sketch, "E262.7", {"start": v(902.97, 12.7) * mm, "mid": v(909.32, 19.05) * mm, "end": v(915.67, 12.7) * mm});
            skArc(sketch, "E262.8", {"start": v(915.67, 12.7) * mm, "mid": v(914.28, 6.35) * mm, "end": v(915.67, 0) * mm});
            skPoint(sketch, "E262.9", {"position": v(886, 12.7) * mm});
            skArc(sketch, "E262.10", {"start": v(814.07, 77.47) * mm, "mid": v(868.85, 54.78) * mm, "end": v(891.54, 0) * mm});
            skArc(sketch, "E262.11", {"start": v(814.07, 69.85) * mm, "mid": v(863.46, 49.4) * mm, "end": v(883.92, 0) * mm});
            skArc(sketch, "E262.12", {"start": v(814.07, 63.5) * mm, "mid": v(858.97, 44.9) * mm, "end": v(877.57, 0) * mm});
            skLineSegment(sketch, "E262.13", {"start": v(814.07, 63.5) * mm, "end": v(814.07, 88.9) * mm});
            skLineSegment(sketch, "E262.14", {"start": v(814.07, 101.6) * mm, "end": v(814.07, 127) * mm});
            skArc(sketch, "E262.15", {"start": v(801.37, 101.6) * mm, "mid": v(807.72, 100.21) * mm, "end": v(814.07, 101.6) * mm});
            skArc(sketch, "E262.16", {"start": v(801.37, 88.9) * mm, "mid": v(807.72, 90.29) * mm, "end": v(814.07, 88.9) * mm});
            skArc(sketch, "E262.17", {"start": v(801.37, 88.9) * mm, "mid": v(795.02, 95.25) * mm, "end": v(801.37, 101.6) * mm});
            skArc(sketch, "E263.MirrorCS", {"start": v(1268.5, 88.9) * mm, "mid": v(1262.14, 90.29) * mm, "end": v(1255.8, 88.9) * mm});
            skArc(sketch, "E264.MirrorCS", {"start": v(1268.5, 101.6) * mm, "mid": v(1262.14, 100.21) * mm, "end": v(1255.8, 101.6) * mm});
            skArc(sketch, "E265.MirrorCS", {"start": v(1154.2, 12.7) * mm, "mid": v(1155.58, 6.35) * mm, "end": v(1154.2, 0) * mm});
            skArc(sketch, "E266.MirrorCS", {"start": v(1268.5, 88.9) * mm, "mid": v(1274.84, 95.25) * mm, "end": v(1268.5, 101.6) * mm});
            skArc(sketch, "E267.MirrorCS", {"start": v(1166.9, 12.7) * mm, "mid": v(1165.5, 6.35) * mm, "end": v(1166.9, 0) * mm});
            skArc(sketch, "E268.MirrorCS", {"start": v(1166.9, 12.7) * mm, "mid": v(1160.54, 19.05) * mm, "end": v(1154.2, 12.7) * mm});
            skLineSegment(sketch, "E269.MirrorCS", {"start": v(1128.8, 0) * mm, "end": v(1154.2, 0) * mm});
            skLineSegment(sketch, "E270.MirrorCS", {"start": v(1255.8, 101.6) * mm, "end": v(1255.8, 127) * mm});
            skLineSegment(sketch, "E271.MirrorCS", {"start": v(1255.8, 63.5) * mm, "end": v(1255.8, 88.9) * mm});
            skLineSegment(sketch, "E272.MirrorCS", {"start": v(1166.9, 0) * mm, "end": v(1192.3, 0) * mm});
            skArc(sketch, "E273.MirrorCS", {"start": v(1255.8, 127) * mm, "mid": v(1166, 89.8) * mm, "end": v(1128.8, 0) * mm});
            skArc(sketch, "E274.MirrorCS", {"start": v(1255.8, 113.03) * mm, "mid": v(1175.87, 79.92) * mm, "end": v(1142.76, 0) * mm});
            skArc(sketch, "E275.MirrorCS", {"start": v(1255.8, 120.65) * mm, "mid": v(1170.48, 85.31) * mm, "end": v(1135.14, 0) * mm});
            skPoint(sketch, "E276.MirrorP", {"position": v(1183.87, 12.7) * mm});
            skPoint(sketch, "E277.MirrorP", {"position": v(1153.4, 12.7) * mm});
            skArc(sketch, "E278.MirrorCS", {"start": v(1255.8, 63.5) * mm, "mid": v(1210.9, 44.9) * mm, "end": v(1192.3, 0) * mm});
            skArc(sketch, "E279.MirrorCS", {"start": v(1255.8, 69.85) * mm, "mid": v(1206.4, 49.4) * mm, "end": v(1185.94, 0) * mm});
            skArc(sketch, "E280.MirrorCS", {"start": v(1255.8, 77.47) * mm, "mid": v(1201.01, 54.78) * mm, "end": v(1178.32, 0) * mm});
            skLineSegment(sketch, "E281", {"start": v(1519.22, 198.47) * mm, "end": v(1519.22, -154.52) * mm});
            skArc(sketch, "E282.MirrorCS", {"start": v(1871.54, 12.7) * mm, "mid": v(1877.9, 19.05) * mm, "end": v(1884.24, 12.7) * mm});
            skLineSegment(sketch, "E283.MirrorCS", {"start": v(1909.64, 0) * mm, "end": v(1884.24, 0) * mm});
            skArc(sketch, "E284.MirrorCS", {"start": v(1884.24, 12.7) * mm, "mid": v(1882.86, 6.35) * mm, "end": v(1884.24, 0) * mm});
            skArc(sketch, "E285.MirrorCS", {"start": v(1871.54, 12.7) * mm, "mid": v(1872.93, 6.35) * mm, "end": v(1871.54, 0) * mm});
            skArc(sketch, "E286.MirrorCS", {"start": v(1769.94, 88.9) * mm, "mid": v(1776.3, 90.29) * mm, "end": v(1782.64, 88.9) * mm});
            skArc(sketch, "E287.MirrorCS", {"start": v(1769.94, 88.9) * mm, "mid": v(1763.6, 95.25) * mm, "end": v(1769.94, 101.6) * mm});
            skArc(sketch, "E288.MirrorCS", {"start": v(1769.94, 101.6) * mm, "mid": v(1776.3, 100.21) * mm, "end": v(1782.64, 101.6) * mm});
            skLineSegment(sketch, "E289.MirrorCS", {"start": v(1782.64, 63.5) * mm, "end": v(1782.64, 88.9) * mm});
            skLineSegment(sketch, "E290.MirrorCS", {"start": v(1782.64, 101.6) * mm, "end": v(1782.64, 127) * mm});
            skLineSegment(sketch, "E291.MirrorCS", {"start": v(1871.54, 0) * mm, "end": v(1846.14, 0) * mm});
            skArc(sketch, "E292.MirrorCS", {"start": v(1782.64, 77.47) * mm, "mid": v(1837.42, 54.78) * mm, "end": v(1860.11, 0) * mm});
            skArc(sketch, "E293.MirrorCS", {"start": v(1782.64, 63.5) * mm, "mid": v(1827.54, 44.9) * mm, "end": v(1846.14, 0) * mm});
            skArc(sketch, "E294.MirrorCS", {"start": v(1782.64, 127) * mm, "mid": v(1872.44, 89.8) * mm, "end": v(1909.64, 0) * mm});
            skArc(sketch, "E295.MirrorCS", {"start": v(1782.64, 120.65) * mm, "mid": v(1867.95, 85.31) * mm, "end": v(1903.3, 0) * mm});
            skPoint(sketch, "E296.MirrorP", {"position": v(1854.57, 12.7) * mm});
            skArc(sketch, "E297.MirrorCS", {"start": v(1782.64, 69.85) * mm, "mid": v(1832.03, 49.4) * mm, "end": v(1852.5, 0) * mm});
            skArc(sketch, "E298.MirrorCS", {"start": v(1782.64, 113.03) * mm, "mid": v(1862.57, 79.92) * mm, "end": v(1895.67, 0) * mm});
            skPoint(sketch, "E299.MirrorP", {"position": v(1885.03, 12.7) * mm});
            skLineSegment(sketch, "E300", {"start": v(2077.79, 229.2) * mm, "end": v(2077.79, -130.23) * mm});
            skArc(sketch, "E301.MirrorCS", {"start": v(2271.33, 12.7) * mm, "mid": v(2272.72, 6.35) * mm, "end": v(2271.33, 0) * mm});
            skArc(sketch, "E302.MirrorCS", {"start": v(2284.03, 12.7) * mm, "mid": v(2277.68, 19.05) * mm, "end": v(2271.33, 12.7) * mm});
            skArc(sketch, "E303.MirrorCS", {"start": v(2284.03, 12.7) * mm, "mid": v(2282.65, 6.35) * mm, "end": v(2284.03, 0) * mm});
            skLineSegment(sketch, "E304.MirrorCS", {"start": v(2372.93, 63.5) * mm, "end": v(2372.93, 88.9) * mm});
            skArc(sketch, "E305.MirrorCS", {"start": v(2385.63, 88.9) * mm, "mid": v(2379.28, 90.29) * mm, "end": v(2372.93, 88.9) * mm});
            skLineSegment(sketch, "E306.MirrorCS", {"start": v(2245.93, 0) * mm, "end": v(2271.33, 0) * mm});
            skArc(sketch, "E307.MirrorCS", {"start": v(2385.63, 101.6) * mm, "mid": v(2379.28, 100.21) * mm, "end": v(2372.93, 101.6) * mm});
            skArc(sketch, "E308.MirrorCS", {"start": v(2385.63, 88.9) * mm, "mid": v(2391.98, 95.25) * mm, "end": v(2385.63, 101.6) * mm});
            skLineSegment(sketch, "E309.MirrorCS", {"start": v(2372.93, 101.6) * mm, "end": v(2372.93, 127) * mm});
            skLineSegment(sketch, "E310.MirrorCS", {"start": v(2284.03, 0) * mm, "end": v(2309.43, 0) * mm});
            skArc(sketch, "E311.MirrorCS", {"start": v(2372.93, 77.47) * mm, "mid": v(2318.15, 54.78) * mm, "end": v(2295.46, 0) * mm});
            skPoint(sketch, "E312.MirrorP", {"position": v(2301, 12.7) * mm});
            skArc(sketch, "E313.MirrorCS", {"start": v(2372.93, 63.5) * mm, "mid": v(2328.03, 44.9) * mm, "end": v(2309.43, 0) * mm});
            skArc(sketch, "E314.MirrorCS", {"start": v(2372.93, 127) * mm, "mid": v(2283.13, 89.8) * mm, "end": v(2245.93, 0) * mm});
            skArc(sketch, "E315.MirrorCS", {"start": v(2372.93, 120.65) * mm, "mid": v(2287.62, 85.31) * mm, "end": v(2252.28, 0) * mm});
            skArc(sketch, "E316.MirrorCS", {"start": v(2372.93, 69.85) * mm, "mid": v(2323.54, 49.4) * mm, "end": v(2303.08, 0) * mm});
            skPoint(sketch, "E317.MirrorP", {"position": v(2270.54, 12.7) * mm});
            skArc(sketch, "E318.MirrorCS", {"start": v(2372.93, 113.03) * mm, "mid": v(2293, 79.92) * mm, "end": v(2259.9, 0) * mm});
            skLineSegment(sketch, "E319", {"start": v(2590.29, 330.34) * mm, "end": v(2590.29, -152.83) * mm});
            skArc(sketch, "E320.MirrorCS", {"start": v(2896.54, 12.7) * mm, "mid": v(2902.89, 19.05) * mm, "end": v(2909.24, 12.7) * mm});
            skLineSegment(sketch, "E321.MirrorCS", {"start": v(2896.54, 0) * mm, "end": v(2871.14, 0) * mm});
            skArc(sketch, "E322.MirrorCS", {"start": v(2909.24, 12.7) * mm, "mid": v(2907.85, 6.35) * mm, "end": v(2909.24, 0) * mm});
            skArc(sketch, "E323.MirrorCS", {"start": v(2896.54, 12.7) * mm, "mid": v(2897.92, 6.35) * mm, "end": v(2896.54, 0) * mm});
            skLineSegment(sketch, "E324.MirrorCS", {"start": v(2934.64, 0) * mm, "end": v(2909.24, 0) * mm});
            skLineSegment(sketch, "E325.MirrorCS", {"start": v(2807.64, 63.5) * mm, "end": v(2807.64, 88.9) * mm});
            skArc(sketch, "E326.MirrorCS", {"start": v(2794.94, 101.6) * mm, "mid": v(2801.29, 100.21) * mm, "end": v(2807.64, 101.6) * mm});
            skArc(sketch, "E327.MirrorCS", {"start": v(2794.94, 88.9) * mm, "mid": v(2801.29, 90.29) * mm, "end": v(2807.64, 88.9) * mm});
            skArc(sketch, "E328.MirrorCS", {"start": v(2794.94, 88.9) * mm, "mid": v(2788.59, 95.25) * mm, "end": v(2794.94, 101.6) * mm});
            skLineSegment(sketch, "E329.MirrorCS", {"start": v(2807.64, 101.6) * mm, "end": v(2807.64, 127) * mm});
            skArc(sketch, "E330.MirrorCS", {"start": v(2807.64, 63.5) * mm, "mid": v(2852.54, 44.9) * mm, "end": v(2871.14, 0) * mm});
            skArc(sketch, "E331.MirrorCS", {"start": v(2807.64, 120.65) * mm, "mid": v(2892.95, 85.31) * mm, "end": v(2928.29, 0) * mm});
            skPoint(sketch, "E332.MirrorP", {"position": v(2910.03, 12.7) * mm});
            skArc(sketch, "E333.MirrorCS", {"start": v(2807.64, 113.03) * mm, "mid": v(2887.56, 79.92) * mm, "end": v(2920.67, 0) * mm});
            skArc(sketch, "E334.MirrorCS", {"start": v(2807.64, 77.47) * mm, "mid": v(2862.42, 54.78) * mm, "end": v(2885.1, 0) * mm});
            skArc(sketch, "E335.MirrorCS", {"start": v(2807.64, 127) * mm, "mid": v(2897.44, 89.8) * mm, "end": v(2934.64, 0) * mm});
            skArc(sketch, "E336.MirrorCS", {"start": v(2807.64, 69.85) * mm, "mid": v(2857.03, 49.4) * mm, "end": v(2877.49, 0) * mm});
            skPoint(sketch, "E337.MirrorP", {"position": v(2879.57, 12.7) * mm});
            skLineSegment(sketch, "E338", {"start": v(1782.64, 120.65) * mm, "end": v(1782.64, 113.03) * mm});
            skLineSegment(sketch, "E339", {"start": v(1782.64, 69.85) * mm, "end": v(1782.64, 77.47) * mm});
            skLineSegment(sketch, "E340", {"start": v(1852.5, 0) * mm, "end": v(1860.11, 0) * mm});
            skLineSegment(sketch, "E341", {"start": v(1895.67, 0) * mm, "end": v(1903.3, 0) * mm});
            skLineSegment(sketch, "E342", {"start": v(2928.29, 0) * mm, "end": v(2920.67, 0) * mm});
            skLineSegment(sketch, "E343", {"start": v(2885.1, 0) * mm, "end": v(2877.49, 0) * mm});
            skLineSegment(sketch, "E344", {"start": v(2807.64, 77.47) * mm, "end": v(2807.64, 69.85) * mm});
            skLineSegment(sketch, "E345", {"start": v(2807.64, 120.65) * mm, "end": v(2807.64, 113.03) * mm});
            skSolve(sketch);
        }
        {
            var Q0;
            {var subQ8=sQuery(id+"F6.wireOp",EDGE,"E284.MirrorCS");Q0=makeQuery(id+"F6.imprint","IMPRINT",FACE,{"disambiguationData":[TD([[makeQuery(id+"F6.imprint","IMPRINT",EDGE,{"derivedFrom":subQ8}),1.0]])]});}
            var Q1;
            {var subQ0=sQuery(id+"F6.wireOp",EDGE,"E294.MirrorCS");Q1=makeQuery(id+"F6.imprint","IMPRINT",FACE,{"disambiguationData":[TD([[makeQuery(id+"F6.imprint","IMPRINT",EDGE,{"derivedFrom":subQ0}),-1.0]])]});}
            var Q2;
            {var subQ0=sQuery(id+"F6.wireOp",EDGE,"E295.MirrorCS");Q2=makeQuery(id+"F6.imprint","IMPRINT",FACE,{"disambiguationData":[TD([[makeQuery(id+"F6.imprint","IMPRINT",EDGE,{"derivedFrom":subQ0}),-1.0]])]});}
            var Q3;
            {var subQ0=sQuery(id+"F6.wireOp",EDGE,"E297.MirrorCS");Q3=makeQuery(id+"F6.imprint","IMPRINT",FACE,{"disambiguationData":[TD([[makeQuery(id+"F6.imprint","IMPRINT",EDGE,{"derivedFrom":subQ0}),1.0]])]});}
            var Q4;
            {var subQ2=sQuery(id+"F6.wireOp",EDGE,"E297.MirrorCS");Q4=makeQuery(id+"F6.imprint","IMPRINT",FACE,{"disambiguationData":[TD([[makeQuery(id+"F6.imprint","IMPRINT",EDGE,{"derivedFrom":subQ2}),-1.0]])]});}
            var Q5;
            Q5=makeQuery(id+"F6.imprint","IMPRINT",FACE,{"disambiguationData":[TD([[makeQuery(id+"F6.imprint","IMPRINT",EDGE,{"derivedFrom":sQuery(id+"F6.wireOp",EDGE,"E320.MirrorCS")}),1.0]])]});
            var Q6;
            {var subQ0=sQuery(id+"F6.wireOp",EDGE,"E336.MirrorCS");Q6=makeQuery(id+"F6.imprint","IMPRINT",FACE,{"disambiguationData":[TD([[makeQuery(id+"F6.imprint","IMPRINT",EDGE,{"derivedFrom":subQ0}),1.0]])]});}
            var Q7;
            {var subQ0=sQuery(id+"F6.wireOp",EDGE,"E330.MirrorCS");Q7=makeQuery(id+"F6.imprint","IMPRINT",FACE,{"disambiguationData":[TD([[makeQuery(id+"F6.imprint","IMPRINT",EDGE,{"derivedFrom":subQ0}),1.0]])]});}
            var Q8;
            {var subQ2=sQuery(id+"F6.wireOp",EDGE,"E331.MirrorCS");Q8=makeQuery(id+"F6.imprint","IMPRINT",FACE,{"disambiguationData":[TD([[makeQuery(id+"F6.imprint","IMPRINT",EDGE,{"derivedFrom":subQ2}),1.0]])]});}
            var Q9;
            {var subQ0=sQuery(id+"F6.wireOp",EDGE,"E331.MirrorCS");Q9=makeQuery(id+"F6.imprint","IMPRINT",FACE,{"disambiguationData":[TD([[makeQuery(id+"F6.imprint","IMPRINT",EDGE,{"derivedFrom":subQ0}),-1.0]])]});}
            var Q10;
            {var subQ5=sQuery(id+"F6.wireOp",EDGE,"E265.MirrorCS");Q10=makeQuery(id+"F6.imprint","IMPRINT",FACE,{"disambiguationData":[TD([[makeQuery(id+"F6.imprint","IMPRINT",EDGE,{"derivedFrom":subQ5}),-1.0]])]});}
            var Q11;
            {var subQ0=sQuery(id+"F6.wireOp",EDGE,"E273.MirrorCS");Q11=makeQuery(id+"F6.imprint","IMPRINT",FACE,{"disambiguationData":[TD([[makeQuery(id+"F6.imprint","IMPRINT",EDGE,{"derivedFrom":subQ0}),1.0]])]});}
            var Q12;
            {var subQ2=sQuery(id+"F6.wireOp",EDGE,"E279.MirrorCS");Q12=makeQuery(id+"F6.imprint","IMPRINT",FACE,{"disambiguationData":[TD([[makeQuery(id+"F6.imprint","IMPRINT",EDGE,{"derivedFrom":subQ2}),1.0]])]});}
            extrude(context, id + "F7", {"entities" : qUnion([Q0, Q1, Q2, Q3, Q4, Q5, Q6, Q7, Q8, Q9, Q10, Q11, Q12]), "depth" : 6.35 * mm});
        }
        {
            var Q0;
            Q0=makeQuery(id+"F7.opExtrude","CAP_FACE",FACE,{"disambiguationData":[OSD([sQuery(id+"F6.wireOp",EDGE,"E284.MirrorCS"),sQuery(id+"F6.wireOp",EDGE,"E285.MirrorCS"),sQuery(id+"F6.wireOp",EDGE,"E282.MirrorCS"),sQuery(id+"F6.wireOp",EDGE,"E283.MirrorCS"),sQuery(id+"F6.wireOp",EDGE,"E288.MirrorCS"),sQuery(id+"F6.wireOp",EDGE,"E286.MirrorCS"),sQuery(id+"F6.wireOp",EDGE,"E287.MirrorCS"),sQuery(id+"F6.wireOp",EDGE,"E290.MirrorCS"),sQuery(id+"F6.wireOp",EDGE,"E289.MirrorCS"),sQuery(id+"F6.wireOp",EDGE,"E291.MirrorCS"),sQuery(id+"F6.wireOp",EDGE,"E294.MirrorCS"),sQuery(id+"F6.wireOp",EDGE,"E293.MirrorCS"),sQuery(id+"F6.wireOp",EDGE,"E339"),sQuery(id+"F6.wireOp",EDGE,"E340"),sQuery(id+"F6.wireOp",EDGE,"E341"),sQuery(id+"F6.wireOp",EDGE,"E338")])],"isStart":false});
            var sketch = newSketch(context, id + "F8", { "sketchPlane" : qUnion([Q0])});
            skArc(sketch, "E346.0", {"start": v(2807.64, 120.65) * mm, "mid": v(2892.95, 85.31) * mm, "end": v(2928.29, 0) * mm});
            skArc(sketch, "E346.1", {"start": v(2807.64, 113.03) * mm, "mid": v(2887.56, 79.92) * mm, "end": v(2920.67, 0) * mm});
            skArc(sketch, "E346.2", {"start": v(2807.64, 77.47) * mm, "mid": v(2862.42, 54.78) * mm, "end": v(2885.1, 0) * mm});
            skArc(sketch, "E346.3", {"start": v(2807.64, 69.85) * mm, "mid": v(2857.03, 49.4) * mm, "end": v(2877.49, 0) * mm});
            skLineSegment(sketch, "E346.4", {"start": v(2807.64, 69.85) * mm, "end": v(2807.64, 77.47) * mm});
            skLineSegment(sketch, "E346.5", {"start": v(2807.64, 113.03) * mm, "end": v(2807.64, 120.65) * mm});
            skLineSegment(sketch, "E346.6", {"start": v(2928.29, 0) * mm, "end": v(2920.67, 0) * mm});
            skLineSegment(sketch, "E346.7", {"start": v(2885.1, 0) * mm, "end": v(2877.49, 0) * mm});
            skPoint(sketch, "E347.orphan", {"position": v(2807.64, 127) * mm});
            skPoint(sketch, "E348.orphan", {"position": v(2807.64, 101.6) * mm});
            skPoint(sketch, "E349.orphan", {"position": v(2807.64, 88.9) * mm});
            skPoint(sketch, "E350.orphan", {"position": v(2807.64, 63.5) * mm});
            skPoint(sketch, "E351.orphan", {"position": v(2909.24, 0) * mm});
            skPoint(sketch, "E352.orphan", {"position": v(2934.64, 0) * mm});
            skPoint(sketch, "E353.orphan", {"position": v(2896.54, 0) * mm});
            skPoint(sketch, "E354.orphan", {"position": v(2871.14, 0) * mm});
            skArc(sketch, "E355.0", {"start": v(1782.64, 120.65) * mm, "mid": v(1867.95, 85.31) * mm, "end": v(1903.3, 0) * mm});
            skArc(sketch, "E355.1", {"start": v(1782.64, 113.03) * mm, "mid": v(1862.57, 79.92) * mm, "end": v(1895.67, 0) * mm});
            skArc(sketch, "E355.2", {"start": v(1782.64, 69.85) * mm, "mid": v(1832.03, 49.4) * mm, "end": v(1852.5, 0) * mm});
            skArc(sketch, "E355.3", {"start": v(1782.64, 77.47) * mm, "mid": v(1837.42, 54.78) * mm, "end": v(1860.11, 0) * mm});
            skLineSegment(sketch, "E355.4", {"start": v(1860.11, 0) * mm, "end": v(1852.5, 0) * mm});
            skLineSegment(sketch, "E355.5", {"start": v(1903.3, 0) * mm, "end": v(1895.67, 0) * mm});
            skLineSegment(sketch, "E355.6", {"start": v(1782.64, 113.03) * mm, "end": v(1782.64, 120.65) * mm});
            skLineSegment(sketch, "E355.7", {"start": v(1782.64, 69.85) * mm, "end": v(1782.64, 77.47) * mm});
            skPoint(sketch, "E356.orphan", {"position": v(1782.64, 127) * mm});
            skPoint(sketch, "E357.orphan", {"position": v(1909.64, 0) * mm});
            skPoint(sketch, "E358.orphan", {"position": v(1884.24, 0) * mm});
            skPoint(sketch, "E359.orphan", {"position": v(1782.64, 101.6) * mm});
            skPoint(sketch, "E360.orphan", {"position": v(1782.64, 88.9) * mm});
            skPoint(sketch, "E361.orphan", {"position": v(1871.54, 0) * mm});
            skPoint(sketch, "E362.orphan", {"position": v(1846.14, 0) * mm});
            skPoint(sketch, "E363.orphan", {"position": v(1782.64, 63.5) * mm});
            skSolve(sketch);
        }
        {
            var Q0;
            Q0=makeQuery(id+"F8.imprint","IMPRINT",FACE,{"disambiguationData":[TD([[makeQuery(id+"F8.imprint","IMPRINT",EDGE,{"derivedFrom":sQuery(id+"F8.wireOp",EDGE,"E355.0")}),-1.0]])]});
            var Q1;
            Q1=makeQuery(id+"F8.imprint","IMPRINT",FACE,{"disambiguationData":[TD([[makeQuery(id+"F8.imprint","IMPRINT",EDGE,{"derivedFrom":sQuery(id+"F8.wireOp",EDGE,"E355.2")}),1.0]])]});
            var Q2;
            Q2=makeQuery(id+"F8.imprint","IMPRINT",FACE,{"disambiguationData":[TD([[makeQuery(id+"F8.imprint","IMPRINT",EDGE,{"derivedFrom":sQuery(id+"F8.wireOp",EDGE,"E346.2")}),-1.0]])]});
            var Q3;
            Q3=makeQuery(id+"F8.imprint","IMPRINT",FACE,{"disambiguationData":[TD([[makeQuery(id+"F8.imprint","IMPRINT",EDGE,{"derivedFrom":sQuery(id+"F8.wireOp",EDGE,"E346.0")}),-1.0]])]});
            extrude(context, id + "F9", {"entities" : qUnion([Q0, Q1, Q2, Q3]), "operationType" : NewBodyOperationType.REMOVE, "oppositeDirection" : true, "depth" : 1.9 * mm});
        }
        {
            var Q0;
            {var subQ0=sQuery(id+"F6.wireOp",EDGE,"E274.MirrorCS");Q0=makeQuery(id+"F6.imprint","IMPRINT",FACE,{"disambiguationData":[TD([[makeQuery(id+"F6.imprint","IMPRINT",EDGE,{"derivedFrom":subQ0}),-1.0]])]});}
            var Q1;
            {var subQ0=sQuery(id+"F6.wireOp",EDGE,"E280.MirrorCS");Q1=makeQuery(id+"F6.imprint","IMPRINT",FACE,{"disambiguationData":[TD([[makeQuery(id+"F6.imprint","IMPRINT",EDGE,{"derivedFrom":subQ0}),1.0]])]});}
            extrude(context, id + "F10", {"entities" : qUnion([Q0, Q1]), "operationType" : NewBodyOperationType.ADD, "depth" : 4.44 * mm});
        }
        {
            var Q0;
            Q0=makeQuery(id+"F1.opExtrude","SWEPT_BODY",BODY,{"disambiguationData":[OSD([sQuery(id+"F0.wireOp",EDGE,"E133.MirrorCS"),sQuery(id+"F0.wireOp",EDGE,"E135.MirrorCS"),sQuery(id+"F0.wireOp",EDGE,"E138.MirrorCS"),sQuery(id+"F0.wireOp",EDGE,"E134.MirrorCS"),sQuery(id+"F0.wireOp",EDGE,"E137.MirrorCS"),sQuery(id+"F0.wireOp",EDGE,"E139.MirrorCS"),sQuery(id+"F0.wireOp",EDGE,"E140.MirrorCS"),sQuery(id+"F0.wireOp",EDGE,"E141.MirrorCS"),sQuery(id+"F0.wireOp",EDGE,"E143.MirrorCS"),sQuery(id+"F0.wireOp",EDGE,"E144.MirrorCS"),sQuery(id+"F0.wireOp",EDGE,"E146.MirrorCS"),sQuery(id+"F0.wireOp",EDGE,"E147.MirrorCS")])]});
            var Q1;
            Q1=makeQuery(id+"F7.opExtrude","SWEPT_BODY",BODY,{"disambiguationData":[OSD([sQuery(id+"F6.wireOp",EDGE,"E265.MirrorCS"),sQuery(id+"F6.wireOp",EDGE,"E268.MirrorCS"),sQuery(id+"F6.wireOp",EDGE,"E267.MirrorCS"),sQuery(id+"F6.wireOp",EDGE,"E263.MirrorCS"),sQuery(id+"F6.wireOp",EDGE,"E266.MirrorCS"),sQuery(id+"F6.wireOp",EDGE,"E264.MirrorCS"),sQuery(id+"F6.wireOp",EDGE,"E271.MirrorCS"),sQuery(id+"F6.wireOp",EDGE,"E272.MirrorCS"),sQuery(id+"F6.wireOp",EDGE,"E269.MirrorCS"),sQuery(id+"F6.wireOp",EDGE,"E270.MirrorCS"),sQuery(id+"F6.wireOp",EDGE,"E274.MirrorCS"),sQuery(id+"F6.wireOp",EDGE,"E280.MirrorCS")])]});
            deleteBodies(context, id + "F11", {"entities" : qUnion([Q0, Q1])});
        }
        {
            var Q0;
            Q0=makeQuery(id+"F7.opExtrude","SWEPT_BODY",BODY,{"disambiguationData":[OSD([sQuery(id+"F6.wireOp",EDGE,"E320.MirrorCS"),sQuery(id+"F6.wireOp",EDGE,"E321.MirrorCS"),sQuery(id+"F6.wireOp",EDGE,"E322.MirrorCS"),sQuery(id+"F6.wireOp",EDGE,"E323.MirrorCS"),sQuery(id+"F6.wireOp",EDGE,"E324.MirrorCS"),sQuery(id+"F6.wireOp",EDGE,"E325.MirrorCS"),sQuery(id+"F6.wireOp",EDGE,"E327.MirrorCS"),sQuery(id+"F6.wireOp",EDGE,"E326.MirrorCS"),sQuery(id+"F6.wireOp",EDGE,"E328.MirrorCS"),sQuery(id+"F6.wireOp",EDGE,"E329.MirrorCS"),sQuery(id+"F6.wireOp",EDGE,"E330.MirrorCS"),sQuery(id+"F6.wireOp",EDGE,"E335.MirrorCS"),sQuery(id+"F6.wireOp",EDGE,"E342"),sQuery(id+"F6.wireOp",EDGE,"E343"),sQuery(id+"F6.wireOp",EDGE,"E344"),sQuery(id+"F6.wireOp",EDGE,"E345")])]});
            deleteBodies(context, id + "F12", {"entities" : qUnion([Q0])});
        }
        {
            var Q0;
            Q0=makeQuery(id+"F1.opExtrude","CAP_EDGE",EDGE,{"disambiguationData":[OSD([sQuery(id+"F0.wireOp",EDGE,"E0")])],"isStart":false});
            var Q1;
            Q1=makeQuery(id+"F1.opExtrude","CAP_EDGE",EDGE,{"disambiguationData":[OSD([sQuery(id+"F0.wireOp",EDGE,"E1.0")])],"isStart":false});
            var Q2;
            Q2=makeQuery(id+"F1.opExtrude","CAP_EDGE",EDGE,{"disambiguationData":[OSD([sQuery(id+"F0.wireOp",EDGE,"E35.MirrorCS")])],"isStart":false});
            var Q3;
            Q3=makeQuery(id+"F1.opExtrude","CAP_EDGE",EDGE,{"disambiguationData":[OSD([sQuery(id+"F0.wireOp",EDGE,"E33.MirrorCS")])],"isStart":false});
            var Q4;
            Q4=makeQuery(id+"F1.opExtrude","CAP_EDGE",EDGE,{"disambiguationData":[OSD([sQuery(id+"F0.wireOp",EDGE,"E129.MirrorCS")])],"isStart":false});
            var Q5;
            Q5=makeQuery(id+"F1.opExtrude","CAP_EDGE",EDGE,{"disambiguationData":[OSD([sQuery(id+"F0.wireOp",EDGE,"E130.MirrorCS")])],"isStart":false});
            var Q6;
            Q6=makeQuery(id+"F7.opExtrude","CAP_EDGE",EDGE,{"disambiguationData":[OSD([sQuery(id+"F6.wireOp",EDGE,"E293.MirrorCS")])],"isStart":false});
            var Q7;
            Q7=makeQuery(id+"F7.opExtrude","CAP_EDGE",EDGE,{"disambiguationData":[OSD([sQuery(id+"F6.wireOp",EDGE,"E294.MirrorCS")])],"isStart":false});
            var Q8;
            Q8=makeQuery(id+"F1.opExtrude","CAP_EDGE",EDGE,{"disambiguationData":[OSD([sQuery(id+"F0.wireOp",EDGE,"E67.MirrorCS")])],"isStart":false});
            var Q9;
            Q9=makeQuery(id+"F1.opExtrude","CAP_EDGE",EDGE,{"disambiguationData":[OSD([sQuery(id+"F0.wireOp",EDGE,"E66.MirrorCS")])],"isStart":false});
            var Q10;
            Q10=makeQuery(id+"F1.opExtrude","CAP_EDGE",EDGE,{"disambiguationData":[OSD([sQuery(id+"F0.wireOp",EDGE,"E70.MirrorCS")])],"isStart":false});
            var Q11;
            Q11=makeQuery(id+"F1.opExtrude","CAP_EDGE",EDGE,{"disambiguationData":[OSD([sQuery(id+"F0.wireOp",EDGE,"E64.MirrorCS")])],"isStart":false});
            var Q12;
            Q12=makeQuery(id+"F1.opExtrude","CAP_EDGE",EDGE,{"disambiguationData":[OSD([sQuery(id+"F0.wireOp",EDGE,"E100.MirrorCS")])],"isStart":false});
            var Q13;
            Q13=makeQuery(id+"F1.opExtrude","CAP_EDGE",EDGE,{"disambiguationData":[OSD([sQuery(id+"F0.wireOp",EDGE,"E112.MirrorCS")])],"isStart":true});
            var Q14;
            Q14=makeQuery(id+"F1.opExtrude","CAP_EDGE",EDGE,{"disambiguationData":[OSD([sQuery(id+"F0.wireOp",EDGE,"E109.MirrorCS")])],"isStart":false});
            var Q15;
            Q15=makeQuery(id+"F1.opExtrude","CAP_EDGE",EDGE,{"disambiguationData":[OSD([sQuery(id+"F0.wireOp",EDGE,"E102.MirrorCS")])],"isStart":false});
            fillet(context, id + "F13", {"entities" : qUnion([Q0, Q1, Q2, Q3, Q4, Q5, Q6, Q7, Q8, Q9, Q10, Q11, Q12, Q13, Q14, Q15]), "radius" : 5.08 * mm, "tangentPropagation" : true, "allowEdgeOverflow" : false});
        }
    });
